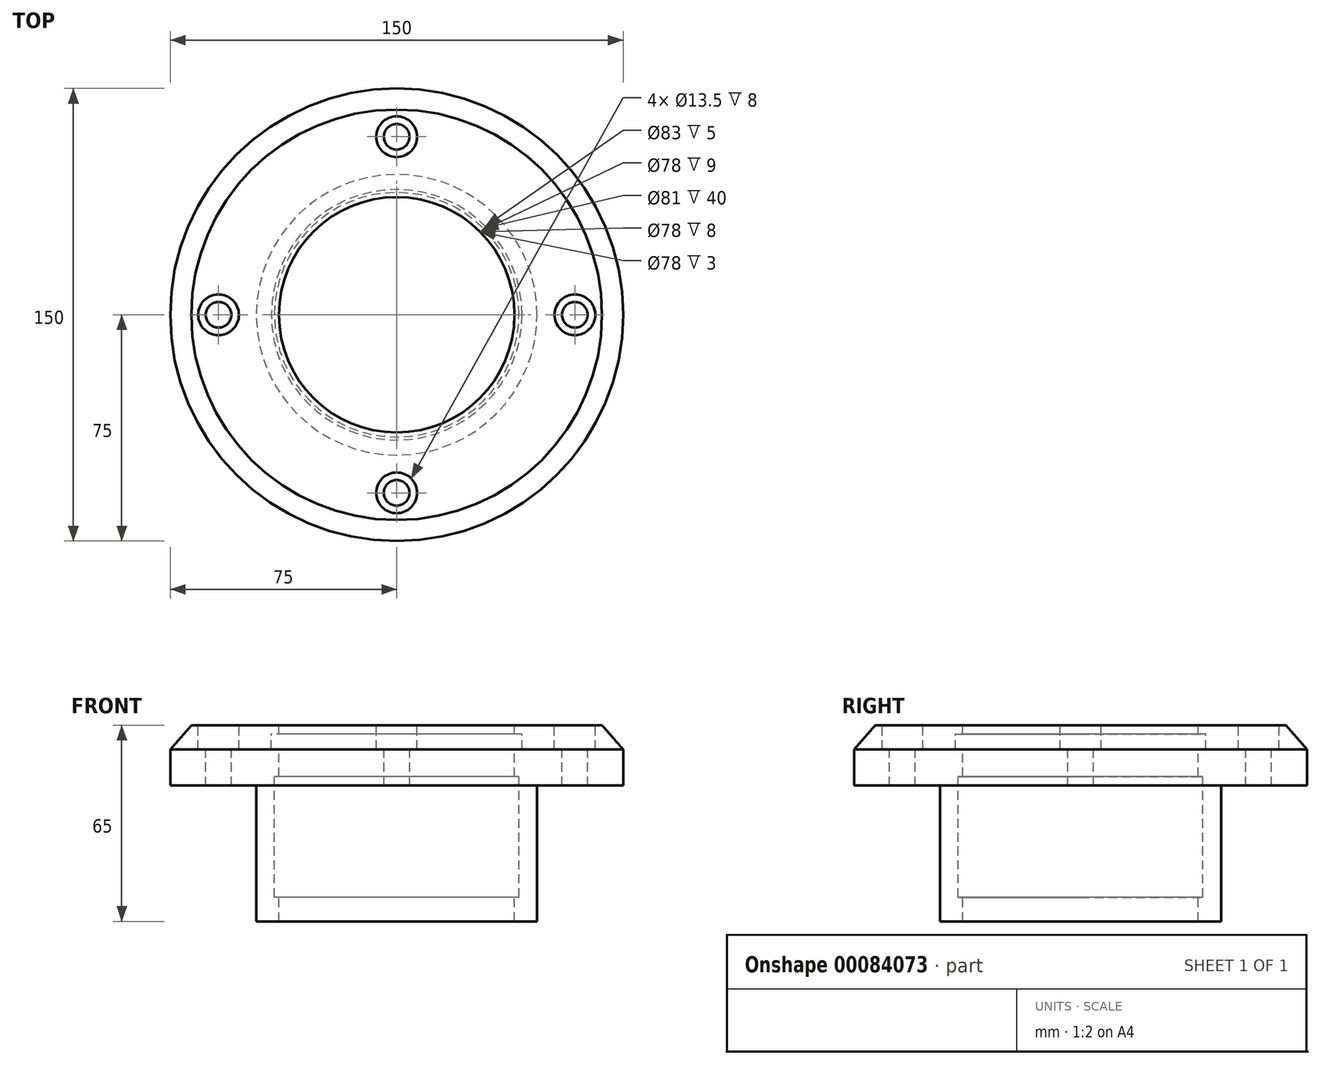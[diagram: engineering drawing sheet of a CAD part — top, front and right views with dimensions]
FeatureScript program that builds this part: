
annotation { "Feature Type Name" : "Feature", "Feature Type Description" : "" }
export const myFeature = defineFeature(function(context is Context, id is Id, definition is map)
    precondition{}
    {
        {
            var Q0;
            Q0=qCreatedBy(makeId("Front.planeOp"),FACE);
            var sketch = newSketch(context, id + "F0", { "sketchPlane" : qUnion([Q0])});
            skLineSegment(sketch, "E0", {"start": v(68, 65) * mm, "end": v(75, 57) * mm});
            skLineSegment(sketch, "E1", {"start": v(75, 57) * mm, "end": v(75, 45) * mm});
            skLineSegment(sketch, "E2", {"start": v(68, 65) * mm, "end": v(39, 65) * mm});
            skLineSegment(sketch, "E3", {"start": v(40.5, 48) * mm, "end": v(39, 48) * mm});
            skLineSegment(sketch, "E4", {"start": v(39, 48) * mm, "end": v(39, 57) * mm});
            skLineSegment(sketch, "E5", {"start": v(39, 57) * mm, "end": v(41.5, 57) * mm});
            skLineSegment(sketch, "E6", {"start": v(41.5, 57) * mm, "end": v(41.5, 62) * mm});
            skLineSegment(sketch, "E7", {"start": v(41.5, 62) * mm, "end": v(39, 62) * mm});
            skLineSegment(sketch, "E8", {"start": v(39, 62) * mm, "end": v(39, 65) * mm});
            skLineSegment(sketch, "E9", {"start": v(40.5, 48) * mm, "end": v(40.5, 8) * mm});
            skLineSegment(sketch, "E10", {"start": v(40.5, 8) * mm, "end": v(39, 8) * mm});
            skLineSegment(sketch, "E11", {"start": v(39, 8) * mm, "end": v(39, 0) * mm});
            skLineSegment(sketch, "E12", {"start": v(46.5, 0) * mm, "end": v(46.5, 45) * mm});
            skLineSegment(sketch, "E13", {"start": v(46.5, 45) * mm, "end": v(75, 45) * mm});
            skLineSegment(sketch, "E14", {"start": v(39, 0) * mm, "end": v(46.5, 0) * mm});
            skLineSegment(sketch, "E15", {"start": v(0, 46.24) * mm, "end": v(0, -18.2) * mm, "construction": true});
            skSolve(sketch);
        }
        {
            var Q0;
            Q0=makeQuery(id+"F0.imprint","IMPRINT",FACE,{"disambiguationData":[TD([[makeQuery(id+"F0.imprint","IMPRINT",EDGE,{"derivedFrom":sQuery(id+"F0.wireOp",EDGE,"E0")}),-1.0]])]});
            var Q1;
            Q1=sQuery(id+"F0.wireOp",EDGE,"E15");
            revolve(context, id + "F1", {"entities" : qUnion([Q0]), "axis" : qUnion([Q1]), "revolveType" : RevolveType.FULL});
        }
        {
            var Q0;
            Q0=qCreatedBy(makeId("Front.planeOp"),FACE);
            var sketch = newSketch(context, id + "F2", { "sketchPlane" : qUnion([Q0])});
            skSolve(sketch);
        }
        {
            var Q0;
            Q0=qCreatedBy(makeId("Top.planeOp"),FACE);
            var Q1;
            Q1 = qBodyType(qCreatedBy(id + "F2" ,EDGE), BodyType.WIRE);
            cPlane(context, id + "F3", {"entities" : qUnion([Q0, Q1]), "cplaneType" : CPlaneType.OFFSET, "offset" : 65 * mm, "width" : 150 * mm, "height" : 150 * mm});
        }
        {
            var Q0;
            Q0=qCreatedBy(id+"F3.planeOp",FACE);
            var sketch = newSketch(context, id + "F4", { "sketchPlane" : qUnion([Q0])});
            skCircle(sketch, "E16", {"center": v(0, 0) * mm, "radius": 59 * mm, "construction": true});
            skCircle(sketch, "E17", {"center": v(0, 59) * mm, "radius": 4.25 * mm});
            skCircle(sketch, "E18", {"center": v(0, 59) * mm, "radius": 6.75 * mm});
            skCircle(sketch, "E19.1.0", {"center": v(-59, 0) * mm, "radius": 6.75 * mm});
            skCircle(sketch, "E19.1.1", {"center": v(-59, 0) * mm, "radius": 4.25 * mm});
            skCircle(sketch, "E19.2.0", {"center": v(0, -59) * mm, "radius": 6.75 * mm});
            skCircle(sketch, "E19.2.1", {"center": v(0, -59) * mm, "radius": 4.25 * mm});
            skCircle(sketch, "E19.3.0", {"center": v(59, 0) * mm, "radius": 6.75 * mm});
            skCircle(sketch, "E19.3.1", {"center": v(59, 0) * mm, "radius": 4.25 * mm});
            skSolve(sketch);
        }
        {
            var Q0;
            Q0=makeQuery(id+"F4.imprint","IMPRINT",FACE,{"disambiguationData":[TD([[makeQuery(id+"F4.imprint","IMPRINT",EDGE,{"derivedFrom":sQuery(id+"F4.wireOp",EDGE,"E17")}),1.0]])]});
            var Q1;
            Q1=makeQuery(id+"F4.imprint","IMPRINT",FACE,{"disambiguationData":[TD([[makeQuery(id+"F4.imprint","IMPRINT",EDGE,{"derivedFrom":sQuery(id+"F4.wireOp",EDGE,"E19.1.1")}),1.0]])]});
            var Q2;
            Q2=makeQuery(id+"F4.imprint","IMPRINT",FACE,{"disambiguationData":[TD([[makeQuery(id+"F4.imprint","IMPRINT",EDGE,{"derivedFrom":sQuery(id+"F4.wireOp",EDGE,"E19.2.1")}),1.0]])]});
            var Q3;
            Q3=makeQuery(id+"F4.imprint","IMPRINT",FACE,{"disambiguationData":[TD([[makeQuery(id+"F4.imprint","IMPRINT",EDGE,{"derivedFrom":sQuery(id+"F4.wireOp",EDGE,"E19.3.1")}),1.0]])]});
            extrude(context, id + "F5", {"entities" : qUnion([Q0, Q1, Q2, Q3]), "operationType" : NewBodyOperationType.REMOVE, "oppositeDirection" : true, "depth" : 25 * mm});
        }
        {
            var Q0;
            Q0=makeQuery(id+"F4.imprint","IMPRINT",FACE,{"disambiguationData":[TD([[makeQuery(id+"F4.imprint","IMPRINT",EDGE,{"derivedFrom":sQuery(id+"F4.wireOp",EDGE,"E17")}),-1.0]])]});
            extrude(context, id + "F6", {"entities" : qUnion([Q0]), "operationType" : NewBodyOperationType.REMOVE, "oppositeDirection" : true, "depth" : 8 * mm});
        }
        {
            var Q0;
            Q0=makeQuery(id+"F4.imprint","IMPRINT",FACE,{"disambiguationData":[TD([[makeQuery(id+"F4.imprint","IMPRINT",EDGE,{"derivedFrom":sQuery(id+"F4.wireOp",EDGE,"E19.1.0")}),1.0]])]});
            var Q1;
            Q1=makeQuery(id+"F4.imprint","IMPRINT",FACE,{"disambiguationData":[TD([[makeQuery(id+"F4.imprint","IMPRINT",EDGE,{"derivedFrom":sQuery(id+"F4.wireOp",EDGE,"E19.3.0")}),1.0]])]});
            var Q2;
            Q2=makeQuery(id+"F4.imprint","IMPRINT",FACE,{"disambiguationData":[TD([[makeQuery(id+"F4.imprint","IMPRINT",EDGE,{"derivedFrom":sQuery(id+"F4.wireOp",EDGE,"E19.2.0")}),1.0]])]});
            extrude(context, id + "F7", {"entities" : qUnion([Q0, Q1, Q2]), "operationType" : NewBodyOperationType.REMOVE, "oppositeDirection" : true, "depth" : 8 * mm});
        }
        {
            var Q0;
            Q0=makeQuery(id+"F4.imprint","IMPRINT",FACE,{"disambiguationData":[TD([[makeQuery(id+"F4.imprint","IMPRINT",EDGE,{"derivedFrom":sQuery(id+"F4.wireOp",EDGE,"E19.2.0")}),1.0]])]});
            var Q1;
            Q1=sQuery(id+"F4.wireOp",EDGE,"E18");
            var Q2;
            Q2=sQuery(id+"F4.wireOp",EDGE,"E19.1.0");
            var Q3;
            Q3=sQuery(id+"F4.wireOp",EDGE,"E19.2.0");
            var Q4;
            Q4=sQuery(id+"F4.wireOp",EDGE,"E19.3.0");
            extrude(context, id + "F8", {"entities" : qUnion([Q0]), "operationType" : NewBodyOperationType.REMOVE, "surfaceEntities" : qUnion([Q1, Q2, Q3, Q4]), "oppositeDirection" : true, "depth" : 8 * mm});
        }
    });
